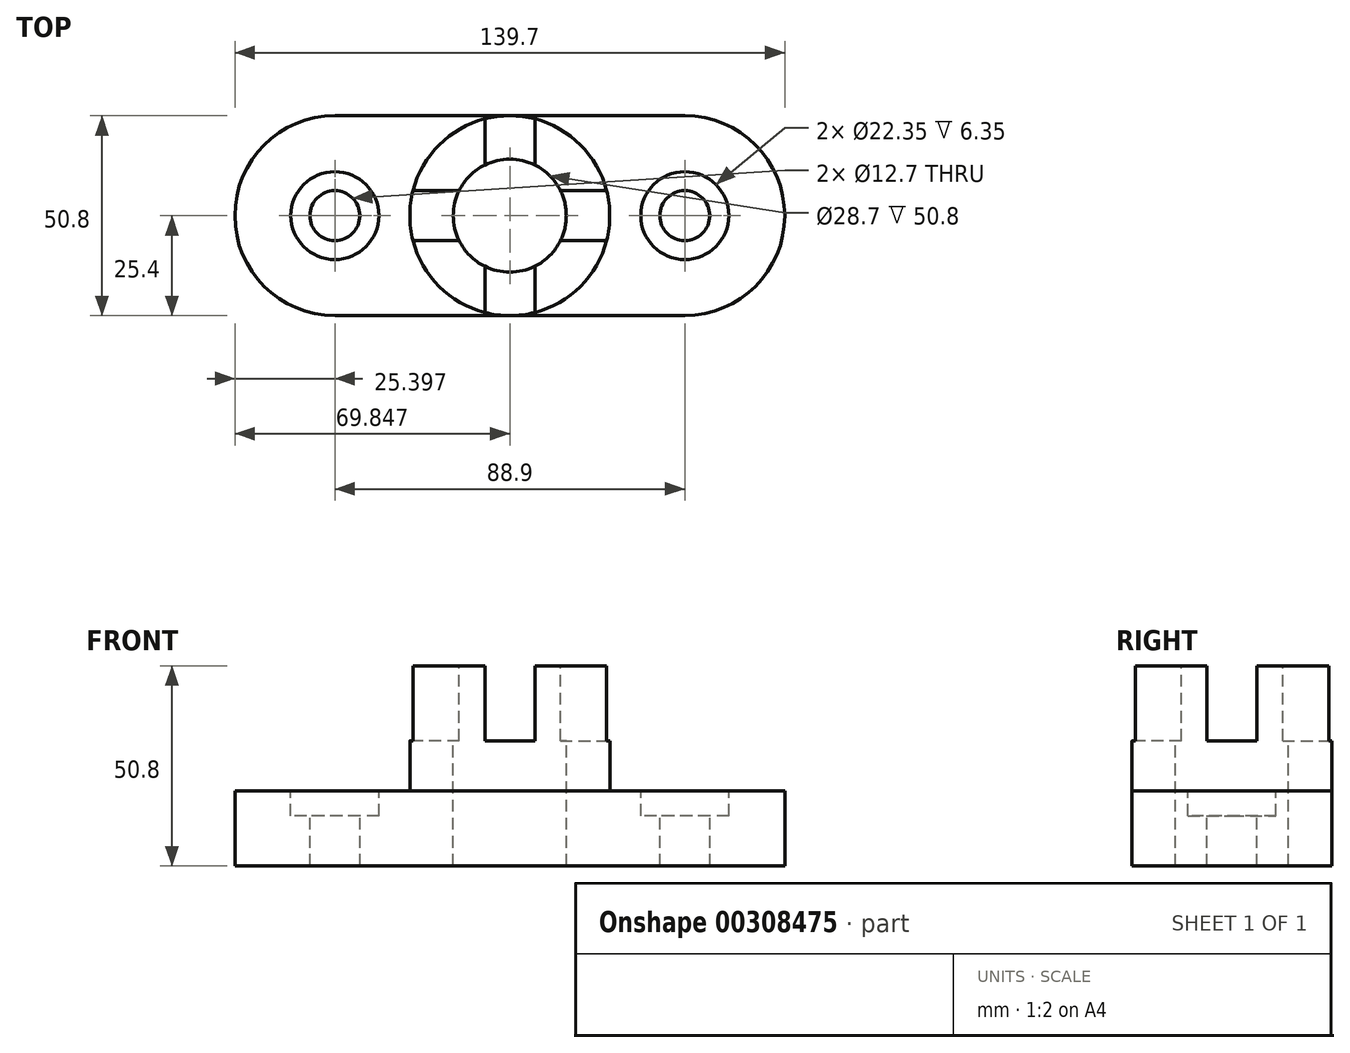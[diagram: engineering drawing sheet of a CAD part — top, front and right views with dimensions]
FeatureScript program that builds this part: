
annotation { "Feature Type Name" : "Feature", "Feature Type Description" : "" }
export const myFeature = defineFeature(function(context is Context, id is Id, definition is map)
    precondition{}
    {
        {
            var Q0;
            Q0=qCreatedBy(makeId("Top.planeOp"),FACE);
            var sketch = newSketch(context, id + "F0", { "sketchPlane" : qUnion([Q0])});
            skLineSegment(sketch, "E0", {"start": v(-40.03, 25.4) * mm, "end": v(48.87, 25.4) * mm});
            skLineSegment(sketch, "E1", {"start": v(48.87, -25.4) * mm, "end": v(-40.03, -25.4) * mm});
            skArc(sketch, "E2", {"start": v(-40.03, 25.4) * mm, "mid": v(-65.43, 0) * mm, "end": v(-40.03, -25.4) * mm});
            skArc(sketch, "E3", {"start": v(48.87, -25.4) * mm, "mid": v(74.27, 0) * mm, "end": v(48.87, 25.4) * mm});
            skSolve(sketch);
        }
        {
            var Q0;
            Q0 = qSketchRegion(id + "F0", true);
            extrude(context, id + "F1", {"entities" : qUnion([Q0]), "depth" : 19.05 * mm});
        }
        {
            var Q0;
            Q0=makeQuery(id+"F1.opExtrude","CAP_FACE",FACE,{"disambiguationData":[OSD([sQuery(id+"F0.wireOp",EDGE,"E0"),sQuery(id+"F0.wireOp",EDGE,"E1"),sQuery(id+"F0.wireOp",EDGE,"E2"),sQuery(id+"F0.wireOp",EDGE,"E3")])],"isStart":false});
            var sketch = newSketch(context, id + "F2", { "sketchPlane" : qUnion([Q0])});
            skCircle(sketch, "E4", {"center": v(4.42, 0) * mm, "radius": 25.4 * mm});
            skSolve(sketch);
        }
        {
            var Q0;
            Q0 = qSketchRegion(id + "F2", true);
            extrude(context, id + "F3", {"entities" : qUnion([Q0]), "operationType" : NewBodyOperationType.ADD, "depth" : 31.75 * mm});
        }
        {
            var Q0;
            Q0=makeQuery(id+"F3.opExtrude","CAP_FACE",FACE,{"disambiguationData":[OSD([sQuery(id+"F2.wireOp",EDGE,"E4")])],"isStart":false});
            var sketch = newSketch(context, id + "F4", { "sketchPlane" : qUnion([Q0])});
            skArc(sketch, "E5", {"start": v(-1.93, 12.87) * mm, "mid": v(-5.73, 10.15) * mm, "end": v(-8.45, 6.35) * mm});
            skLineSegment(sketch, "E6", {"start": v(4.42, 29.21) * mm, "end": v(4.42, -37.65) * mm, "construction": true});
            skLineSegment(sketch, "E7", {"start": v(-28.2, 0) * mm, "end": v(42.06, 0) * mm, "construction": true});
            skLineSegment(sketch, "E8", {"start": v(-1.93, 24.6) * mm, "end": v(-1.93, 12.87) * mm});
            skLineSegment(sketch, "E9", {"start": v(10.77, -24.6) * mm, "end": v(10.77, -12.87) * mm});
            skLineSegment(sketch, "E10.trimOffspring", {"start": v(10.77, 12.87) * mm, "end": v(10.77, 24.6) * mm});
            skLineSegment(sketch, "E11.trimOffspring", {"start": v(-1.93, -12.87) * mm, "end": v(-1.93, -24.6) * mm});
            skArc(sketch, "E12.trimOffspring", {"start": v(10.77, -12.87) * mm, "mid": v(14.56, -10.15) * mm, "end": v(17.29, -6.35) * mm});
            skLineSegment(sketch, "E13", {"start": v(29.01, 6.35) * mm, "end": v(17.29, 6.35) * mm});
            skLineSegment(sketch, "E14", {"start": v(-20.18, -6.35) * mm, "end": v(-8.45, -6.35) * mm});
            skLineSegment(sketch, "E15.trimOffspring", {"start": v(-8.45, 6.35) * mm, "end": v(-20.18, 6.35) * mm});
            skLineSegment(sketch, "E16.trimOffspring", {"start": v(17.29, -6.35) * mm, "end": v(29.01, -6.35) * mm});
            skArc(sketch, "E17.trimOffspring", {"start": v(-8.45, -6.35) * mm, "mid": v(-5.73, -10.15) * mm, "end": v(-1.93, -12.87) * mm});
            skArc(sketch, "E18.trimOffspring", {"start": v(17.29, 6.35) * mm, "mid": v(14.56, 10.15) * mm, "end": v(10.77, 12.87) * mm});
            skCircle(sketch, "E19", {"center": v(4.42, 0) * mm, "radius": 25.4 * mm});
            skSolve(sketch);
        }
        {
            var Q0;
            Q0=makeQuery(id+"F4.imprint","IMPRINT",FACE,{"disambiguationData":[TD([[makeQuery(id+"F4.imprint","IMPRINT",EDGE,{"derivedFrom":sQuery(id+"F4.wireOp",EDGE,"E5")}),1.0]])]});
            extrude(context, id + "F5", {"entities" : qUnion([Q0]), "operationType" : NewBodyOperationType.REMOVE, "oppositeDirection" : true, "depth" : 19.05 * mm});
        }
        {
            var Q0;
            Q0=makeQuery(id+"F5.boolean.opBoolean","COPY",FACE,{"derivedFrom":makeQuery(id+"F5.opExtrude","CAP_FACE",FACE,{"disambiguationData":[OSD([sQuery(id+"F4.wireOp",EDGE,"E5"),sQuery(id+"F4.wireOp",EDGE,"E8"),sQuery(id+"F4.wireOp",EDGE,"E9"),sQuery(id+"F4.wireOp",EDGE,"E10.trimOffspring"),sQuery(id+"F4.wireOp",EDGE,"E11.trimOffspring"),sQuery(id+"F4.wireOp",EDGE,"E12.trimOffspring"),sQuery(id+"F4.wireOp",EDGE,"E13"),sQuery(id+"F4.wireOp",EDGE,"E14"),sQuery(id+"F4.wireOp",EDGE,"E15.trimOffspring"),sQuery(id+"F4.wireOp",EDGE,"E16.trimOffspring"),sQuery(id+"F4.wireOp",EDGE,"E17.trimOffspring"),sQuery(id+"F4.wireOp",EDGE,"E18.trimOffspring"),sQuery(id+"F4.wireOp",EDGE,"E19")])],"isStart":false})});
            var sketch = newSketch(context, id + "F6", { "sketchPlane" : qUnion([Q0])});
            skCircle(sketch, "E20", {"center": v(4.42, 0) * mm, "radius": 14.35 * mm});
            skSolve(sketch);
        }
        {
            var Q0;
            Q0 = qSketchRegion(id + "F6", true);
            extrude(context, id + "F7", {"entities" : qUnion([Q0]), "operationType" : NewBodyOperationType.REMOVE, "endBound" : BoundingType.THROUGH_ALL, "oppositeDirection" : true, "depth" : 25.4 * mm});
        }
        {
            var Q0;
            {var subQ0=sQuery(id+"F0.wireOp",EDGE,"E2");var subQ1=sQuery(id+"F0.wireOp",EDGE,"E1");var subQ2=sQuery(id+"F0.wireOp",EDGE,"E0");var subQ3=makeQuery(id+"F1.opExtrude","CAP_FACE",FACE,{"disambiguationData":[OSD([subQ2,subQ1,subQ0,sQuery(id+"F0.wireOp",EDGE,"E3")])],"isStart":false});Q0=makeQuery(id+"F3.boolean.opBoolean","SPLIT",FACE,{"disambiguationData":[TD([makeQuery(id+"F1.opExtrude","SWEPT_FACE",FACE,{"disambiguationData":[OSD([subQ0])]})])],"derivedFrom":subQ3});}
            var sketch = newSketch(context, id + "F8", { "sketchPlane" : qUnion([Q0])});
            skCircle(sketch, "E21", {"center": v(-40.03, 0) * mm, "radius": 11.18 * mm});
            skCircle(sketch, "E22", {"center": v(48.87, 0) * mm, "radius": 11.18 * mm});
            skSolve(sketch);
        }
        {
            var Q0;
            Q0 = qSketchRegion(id + "F8", true);
            extrude(context, id + "F9", {"entities" : qUnion([Q0]), "operationType" : NewBodyOperationType.REMOVE, "oppositeDirection" : true, "depth" : 6.35 * mm});
        }
        {
            var Q0;
            Q0=makeQuery(id+"F9.boolean.opBoolean","COPY",FACE,{"derivedFrom":makeQuery(id+"F9.opExtrude","CAP_FACE",FACE,{"disambiguationData":[OSD([sQuery(id+"F8.wireOp",EDGE,"E21")])],"isStart":false})});
            var sketch = newSketch(context, id + "F10", { "sketchPlane" : qUnion([Q0])});
            skCircle(sketch, "E23", {"center": v(-40.03, 0) * mm, "radius": 6.35 * mm});
            skCircle(sketch, "E24", {"center": v(48.87, 0) * mm, "radius": 6.35 * mm});
            skSolve(sketch);
        }
        {
            var Q0;
            Q0 = qSketchRegion(id + "F10", true);
            extrude(context, id + "F11", {"entities" : qUnion([Q0]), "operationType" : NewBodyOperationType.REMOVE, "endBound" : BoundingType.THROUGH_ALL, "oppositeDirection" : true, "depth" : 25.4 * mm});
        }
    });
